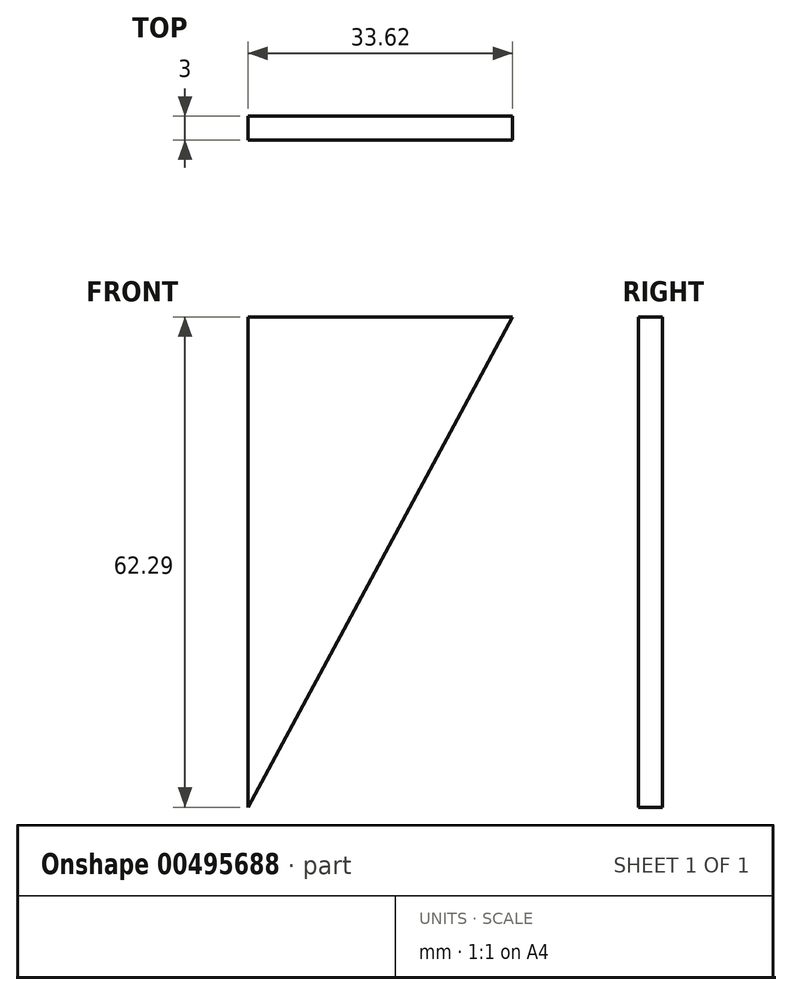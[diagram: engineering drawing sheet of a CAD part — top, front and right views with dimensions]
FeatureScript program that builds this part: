
annotation { "Feature Type Name" : "Feature", "Feature Type Description" : "" }
export const myFeature = defineFeature(function(context is Context, id is Id, definition is map)
    precondition{}
    {
        {
            var Q0;
            Q0=qCreatedBy(makeId("Front.planeOp"),FACE);
            var sketch = newSketch(context, id + "F0", { "sketchPlane" : qUnion([Q0])});
            skLineSegment(sketch, "E0", {"start": v(-35.78, -21.69) * mm, "end": v(-35.78, 40.6) * mm});
            skLineSegment(sketch, "E1", {"start": v(-35.78, 40.6) * mm, "end": v(-2.16, 40.6) * mm});
            skLineSegment(sketch, "E2", {"start": v(-35.78, -21.69) * mm, "end": v(-2.16, 40.6) * mm});
            skSolve(sketch);
        }
        {
            var Q0;
            Q0 = qSketchRegion(id + "F0", true);
            extrude(context, id + "F1", {"entities" : qUnion([Q0]), "depth" : 3 * mm});
        }
    });
